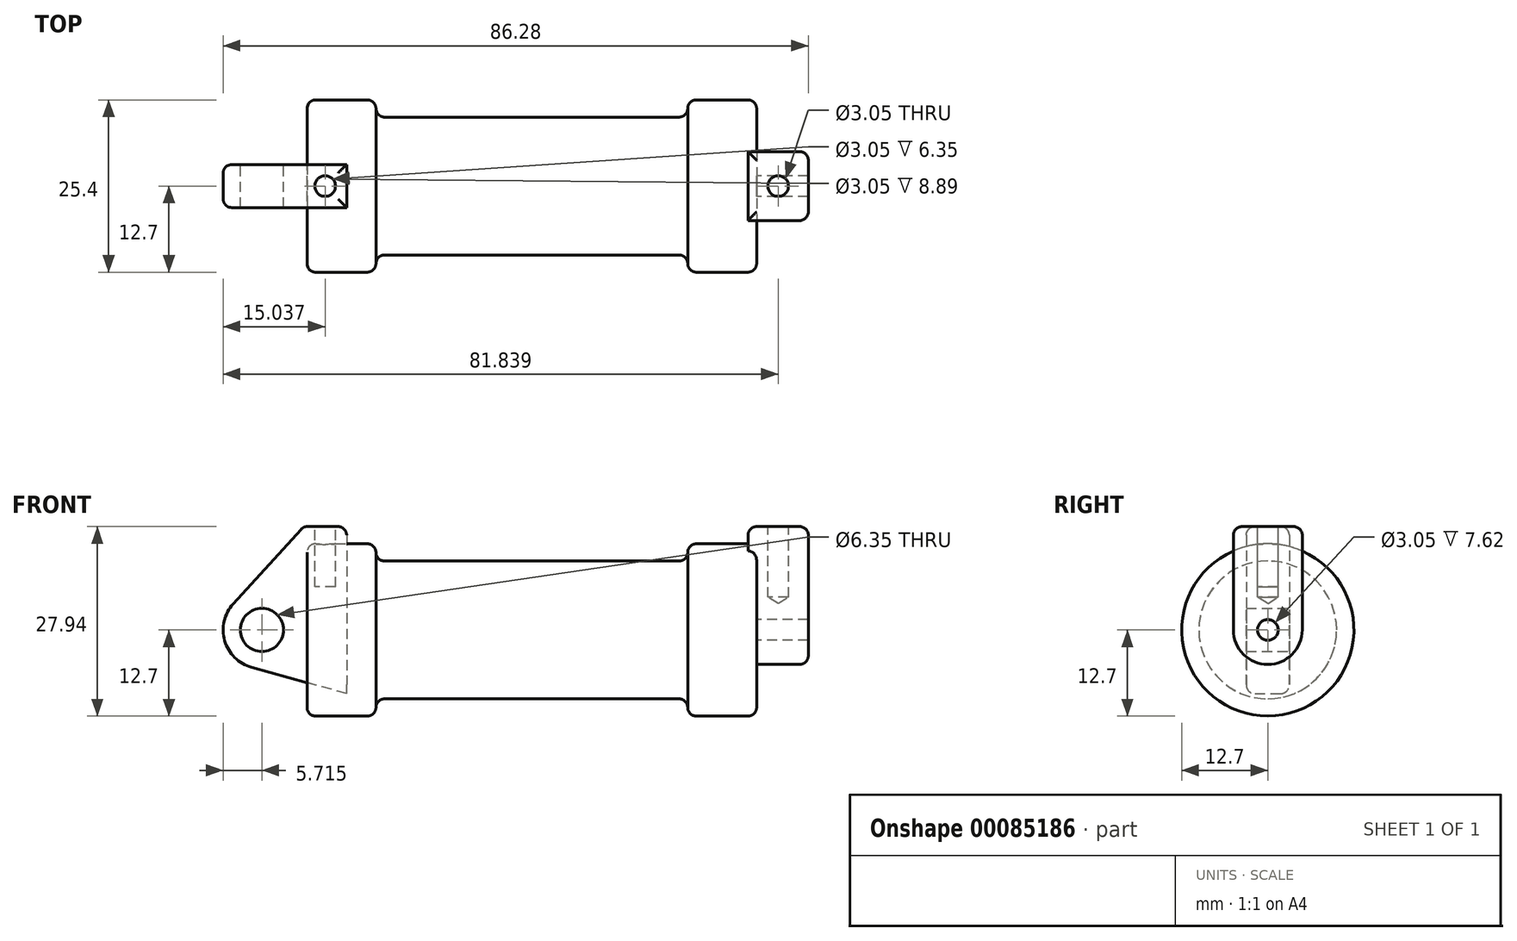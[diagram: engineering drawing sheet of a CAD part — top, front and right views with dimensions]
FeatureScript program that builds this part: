
annotation { "Feature Type Name" : "Feature", "Feature Type Description" : "" }
export const myFeature = defineFeature(function(context is Context, id is Id, definition is map)
    precondition{}
    {
        {
            var Q0;
            Q0=qCreatedBy(makeId("Front.planeOp"),FACE);
            var sketch = newSketch(context, id + "F0", { "sketchPlane" : qUnion([Q0])});
            skLineSegment(sketch, "E0", {"start": v(0, 0) * mm, "end": v(0, 12.7) * mm});
            skLineSegment(sketch, "E1", {"start": v(0, 12.7) * mm, "end": v(10.16, 12.7) * mm});
            skLineSegment(sketch, "E2", {"start": v(10.16, 12.7) * mm, "end": v(10.16, 10.16) * mm});
            skLineSegment(sketch, "E3", {"start": v(10.16, 10.16) * mm, "end": v(56.13, 10.16) * mm});
            skLineSegment(sketch, "E4", {"start": v(56.13, 10.16) * mm, "end": v(56.13, 12.7) * mm});
            skLineSegment(sketch, "E5", {"start": v(56.13, 12.7) * mm, "end": v(66.3, 12.7) * mm});
            skLineSegment(sketch, "E6", {"start": v(66.3, 12.7) * mm, "end": v(66.3, 0) * mm});
            skLineSegment(sketch, "E7", {"start": v(66.3, 0) * mm, "end": v(0, 0) * mm});
            skLineSegment(sketch, "E8", {"start": v(5.84, 15.24) * mm, "end": v(-0.5, 15.24) * mm});
            skLineSegment(sketch, "E9", {"start": v(-0.5, 15.24) * mm, "end": v(-10.88, 3.85) * mm});
            skLineSegment(sketch, "E10", {"start": v(0, 0) * mm, "end": v(-6.65, 0) * mm});
            skCircle(sketch, "E11", {"center": v(-6.65, 0) * mm, "radius": 5.72 * mm});
            skCircle(sketch, "E12", {"center": v(-6.65, 0) * mm, "radius": 3.18 * mm});
            skLineSegment(sketch, "E13", {"start": v(5.84, 15.24) * mm, "end": v(5.84, -9.4) * mm});
            skLineSegment(sketch, "E14", {"start": v(5.84, -9.4) * mm, "end": v(-8.18, -5.5) * mm});
            skSolve(sketch);
        }
        {
            var Q0;
            {var subQ3=sQuery(id+"F0.wireOp",EDGE,"E0");Q0=makeQuery(id+"F0.imprint","IMPRINT",FACE,{"disambiguationData":[TD([[makeQuery(id+"F0.imprint","IMPRINT",EDGE,{"derivedFrom":subQ3}),1.0]])]});}
            var Q1;
            {var subQ4=sQuery(id+"F0.wireOp",EDGE,"E12");Q1=makeQuery(id+"F0.imprint","IMPRINT",FACE,{"disambiguationData":[TD([[makeQuery(id+"F0.imprint","IMPRINT",EDGE,{"derivedFrom":subQ4}),-1.0]])]});}
            var Q2;
            {var subQ0=sQuery(id+"F0.wireOp",EDGE,"E14");Q2=makeQuery(id+"F0.imprint","IMPRINT",FACE,{"disambiguationData":[TD([[makeQuery(id+"F0.imprint","IMPRINT",EDGE,{"derivedFrom":subQ0}),-1.0]])]});}
            extrude(context, id + "F1", {"entities" : qUnion([Q0, Q1, Q2]), "endBound" : BoundingType.SYMMETRIC, "depth" : 6.35 * mm});
        }
        {
            var Q0;
            {var subQ0=sQuery(id+"F0.wireOp",EDGE,"E0");Q0=makeQuery(id+"F0.imprint","IMPRINT",FACE,{"disambiguationData":[TD([[makeQuery(id+"F0.imprint","IMPRINT",EDGE,{"derivedFrom":subQ0}),-1.0]])]});}
            extrude(context, id + "F2", {"entities" : qUnion([Q0]), "operationType" : NewBodyOperationType.ADD, "endBound" : BoundingType.SYMMETRIC, "depth" : 6.35 * mm});
        }
        {
            var Q0;
            {var subQ0=sQuery(id+"F0.wireOp",EDGE,"E2");Q0=makeQuery(id+"F0.imprint","IMPRINT",FACE,{"disambiguationData":[TD([[makeQuery(id+"F0.imprint","IMPRINT",EDGE,{"derivedFrom":subQ0}),-1.0]])]});}
            var Q1;
            {var subQ0=sQuery(id+"F0.wireOp",EDGE,"E0");Q1=makeQuery(id+"F0.imprint","IMPRINT",FACE,{"disambiguationData":[TD([[makeQuery(id+"F0.imprint","IMPRINT",EDGE,{"derivedFrom":subQ0}),-1.0]])]});}
            var Q2;
            Q2=sQuery(id+"F0.wireOp",EDGE,"E7");
            revolve(context, id + "F3", {"entities" : qUnion([Q0, Q1]), "axis" : qUnion([Q2]), "revolveType" : RevolveType.FULL});
        }
        {
            var Q0;
            Q0=makeQuery(id+"F3.opRevolve","SWEPT_FACE",FACE,{"disambiguationData":[OSD([sQuery(id+"F0.wireOp",EDGE,"E6")])]});
            var sketch = newSketch(context, id + "F4", { "sketchPlane" : qUnion([Q0])});
            skCircle(sketch, "E15", {"center": v(0, 0) * mm, "radius": 1.52 * mm});
            skCircle(sketch, "E16", {"center": v(0, 0) * mm, "radius": 5.08 * mm});
            skLineSegment(sketch, "E17", {"start": v(-5.08, 0) * mm, "end": v(-5.08, 15.24) * mm});
            skLineSegment(sketch, "E18", {"start": v(5.08, 0) * mm, "end": v(5.08, 15.24) * mm});
            skLineSegment(sketch, "E19", {"start": v(-5.08, 15.24) * mm, "end": v(5.08, 15.24) * mm});
            skSolve(sketch);
        }
        {
            var Q0;
            Q0 = qSketchRegion(id + "F4", true);
            extrude(context, id + "F5", {"entities" : qUnion([Q0]), "operationType" : NewBodyOperationType.ADD, "depth" : 7.62 * mm});
        }
        {
            var Q0;
            Q0=makeQuery(id+"F5.opExtrude","CAP_FACE",FACE,{"disambiguationData":[OSD([sQuery(id+"F4.wireOp",EDGE,"E15"),sQuery(id+"F4.wireOp",EDGE,"E16"),sQuery(id+"F4.wireOp",EDGE,"E17"),sQuery(id+"F4.wireOp",EDGE,"E18"),sQuery(id+"F4.wireOp",EDGE,"E19")])],"isStart":true});
            extrude(context, id + "F6", {"entities" : qUnion([Q0]), "operationType" : NewBodyOperationType.ADD, "depth" : 1.27 * mm});
        }
        {
            var Q0;
            {var subQ0=sQuery(id+"F4.wireOp",EDGE,"E19");Q0=makeQuery(id+"F6.boolean.opBoolean","MERGE",FACE,{"derivedFrom":[makeQuery(id+"F5.opExtrude","SWEPT_FACE",FACE,{"disambiguationData":[OSD([subQ0])]}),makeQuery(id+"F6.opExtrude","SWEPT_FACE",FACE,{"disambiguationData":[OSD([subQ0])]})]});}
            var sketch = newSketch(context, id + "F7", { "sketchPlane" : qUnion([Q0])});
            skLineSegment(sketch, "E20", {"start": v(65.02, 0) * mm, "end": v(73.91, 0) * mm, "construction": true});
            skCircle(sketch, "E21", {"center": v(69.47, 0) * mm, "radius": 1.52 * mm});
            skSolve(sketch);
        }
        {
            var Q0;
            Q0=sQuery(id+"F7.wireOp",VERTEX,"E21.center");
            var Q1;
            Q1=makeQuery(id+"F3.opRevolve","SWEPT_BODY",BODY,{"disambiguationData":[OSD([sQuery(id+"F0.wireOp",EDGE,"E0"),sQuery(id+"F0.wireOp",EDGE,"E1"),sQuery(id+"F0.wireOp",EDGE,"E2"),sQuery(id+"F0.wireOp",EDGE,"E3"),sQuery(id+"F0.wireOp",EDGE,"E4"),sQuery(id+"F0.wireOp",EDGE,"E5"),sQuery(id+"F0.wireOp",EDGE,"E6"),sQuery(id+"F0.wireOp",EDGE,"E7")])]});
            hole(context, id + "F8", {"style" : HoleStyle.SIMPLE, "endStyle" : HoleEndStyle.BLIND, "holeDiameter" : 3.05 * mm, "holeDepth" : 10.4 * mm, "locations" : qUnion([Q0]), "scope" : qUnion([Q1])});
        }
        {
            var Q0;
            Q0=makeQuery(id+"F1.opExtrude","SWEPT_FACE",FACE,{"disambiguationData":[OSD([sQuery(id+"F0.wireOp",EDGE,"E8")])]});
            var sketch = newSketch(context, id + "F9", { "sketchPlane" : qUnion([Q0])});
            skLineSegment(sketch, "E22", {"start": v(-0.5, 3.18) * mm, "end": v(5.84, -3.18) * mm, "construction": true});
            skCircle(sketch, "E23", {"center": v(2.67, 0) * mm, "radius": 1.52 * mm});
            skSolve(sketch);
        }
        {
            var Q0;
            Q0=makeQuery(id+"F3.opRevolve","SWEPT_FACE",FACE,{"disambiguationData":[OSD([sQuery(id+"F0.wireOp",EDGE,"E4")])]});
            fillet(context, id + "F10", {"entities" : qUnion([Q0]), "radius" : 1.27 * mm, "tangentPropagation" : true, "allowEdgeOverflow" : false});
        }
        {
            var Q0;
            Q0=makeQuery(id+"F3.opRevolve","SWEPT_FACE",FACE,{"disambiguationData":[OSD([sQuery(id+"F0.wireOp",EDGE,"E2")])]});
            fillet(context, id + "F11", {"entities" : qUnion([Q0]), "radius" : 1.27 * mm, "tangentPropagation" : true, "allowEdgeOverflow" : false});
        }
        {
            var Q0;
            Q0=makeQuery(id+"F3.opRevolve","SWEPT_FACE",FACE,{"disambiguationData":[OSD([sQuery(id+"F0.wireOp",EDGE,"E0")])]});
            fillet(context, id + "F12", {"entities" : qUnion([Q0]), "radius" : 1.27 * mm, "tangentPropagation" : true, "allowEdgeOverflow" : false});
        }
        {
            var Q0;
            Q0=makeQuery(id+"F5.boolean.opBoolean","SPLIT",EDGE,{"disambiguationData":[OD(1.0)],"derivedFrom":makeQuery(id+"F3.opRevolve","SWEPT_EDGE",EDGE,{"disambiguationData":[OSD([sQuery(id+"F0.wireOp",EDGE,"E5"),sQuery(id+"F0.wireOp",EDGE,"E6")])]})});
            fillet(context, id + "F13", {"entities" : qUnion([Q0]), "radius" : 1.27 * mm, "tangentPropagation" : true, "allowEdgeOverflow" : false});
        }
        {
            var Q0;
            Q0=makeQuery(id+"F1.opExtrude","SWEPT_EDGE",EDGE,{"disambiguationData":[OSD([sQuery(id+"F0.wireOp",EDGE,"E8"),sQuery(id+"F0.wireOp",EDGE,"E13")])]});
            var Q1;
            Q1=makeQuery(id+"F1.opExtrude","CAP_EDGE",EDGE,{"disambiguationData":[OSD([sQuery(id+"F0.wireOp",EDGE,"E8")])],"isStart":false});
            var Q2;
            Q2=makeQuery(id+"F1.opExtrude","SWEPT_EDGE",EDGE,{"disambiguationData":[OSD([sQuery(id+"F0.wireOp",EDGE,"E8"),sQuery(id+"F0.wireOp",EDGE,"E9")])]});
            var Q3;
            Q3=makeQuery(id+"F1.opExtrude","CAP_EDGE",EDGE,{"disambiguationData":[OSD([sQuery(id+"F0.wireOp",EDGE,"E8")])],"isStart":true});
            var Q4;
            Q4=makeQuery(id+"F1.opExtrude","CAP_EDGE",EDGE,{"disambiguationData":[OSD([sQuery(id+"F0.wireOp",EDGE,"E9")])],"isStart":false});
            var Q5;
            Q5=makeQuery(id+"F1.opExtrude","CAP_EDGE",EDGE,{"disambiguationData":[OSD([sQuery(id+"F0.wireOp",EDGE,"E9")])],"isStart":true});
            var Q6;
            Q6=makeQuery(id+"F5.opExtrude","CAP_EDGE",EDGE,{"disambiguationData":[OSD([sQuery(id+"F4.wireOp",EDGE,"E17")])],"isStart":false});
            var Q7;
            {var subQ0=sQuery(id+"F4.wireOp",EDGE,"E19");var subQ1=sQuery(id+"F4.wireOp",EDGE,"E17");Q7=makeQuery(id+"F6.boolean.opBoolean","MERGE",EDGE,{"derivedFrom":[makeQuery(id+"F5.opExtrude","SWEPT_EDGE",EDGE,{"disambiguationData":[OSD([subQ1,subQ0])]}),makeQuery(id+"F6.opExtrude","SWEPT_EDGE",EDGE,{"disambiguationData":[OSD([subQ1,subQ0])]})]});}
            var Q8;
            {var subQ0=sQuery(id+"F4.wireOp",EDGE,"E19");var subQ1=sQuery(id+"F4.wireOp",EDGE,"E18");Q8=makeQuery(id+"F6.boolean.opBoolean","MERGE",EDGE,{"derivedFrom":[makeQuery(id+"F5.opExtrude","SWEPT_EDGE",EDGE,{"disambiguationData":[OSD([subQ1,subQ0])]}),makeQuery(id+"F6.opExtrude","SWEPT_EDGE",EDGE,{"disambiguationData":[OSD([subQ1,subQ0])]})]});}
            var Q9;
            Q9=makeQuery(id+"F5.opExtrude","CAP_EDGE",EDGE,{"disambiguationData":[OSD([sQuery(id+"F4.wireOp",EDGE,"E19")])],"isStart":false});
            var Q10;
            Q10=makeQuery(id+"F6.opExtrude","CAP_EDGE",EDGE,{"disambiguationData":[OSD([sQuery(id+"F4.wireOp",EDGE,"E19")])],"isStart":false});
            fillet(context, id + "F14", {"entities" : qUnion([Q0, Q1, Q2, Q3, Q4, Q5, Q6, Q7, Q8, Q9, Q10]), "radius" : 1.27 * mm, "tangentPropagation" : true, "allowEdgeOverflow" : false});
        }
        {
            var Q0;
            Q0=makeQuery(id+"F9.imprint","IMPRINT",FACE,{"disambiguationData":[TD([[makeQuery(id+"F9.imprint","IMPRINT",EDGE,{"derivedFrom":sQuery(id+"F9.wireOp",EDGE,"E23")}),1.0]])]});
            extrude(context, id + "F15", {"entities" : qUnion([Q0]), "operationType" : NewBodyOperationType.REMOVE, "endBound" : BoundingType.SYMMETRIC, "oppositeDirection" : true, "depth" : 17.78 * mm});
        }
    });
